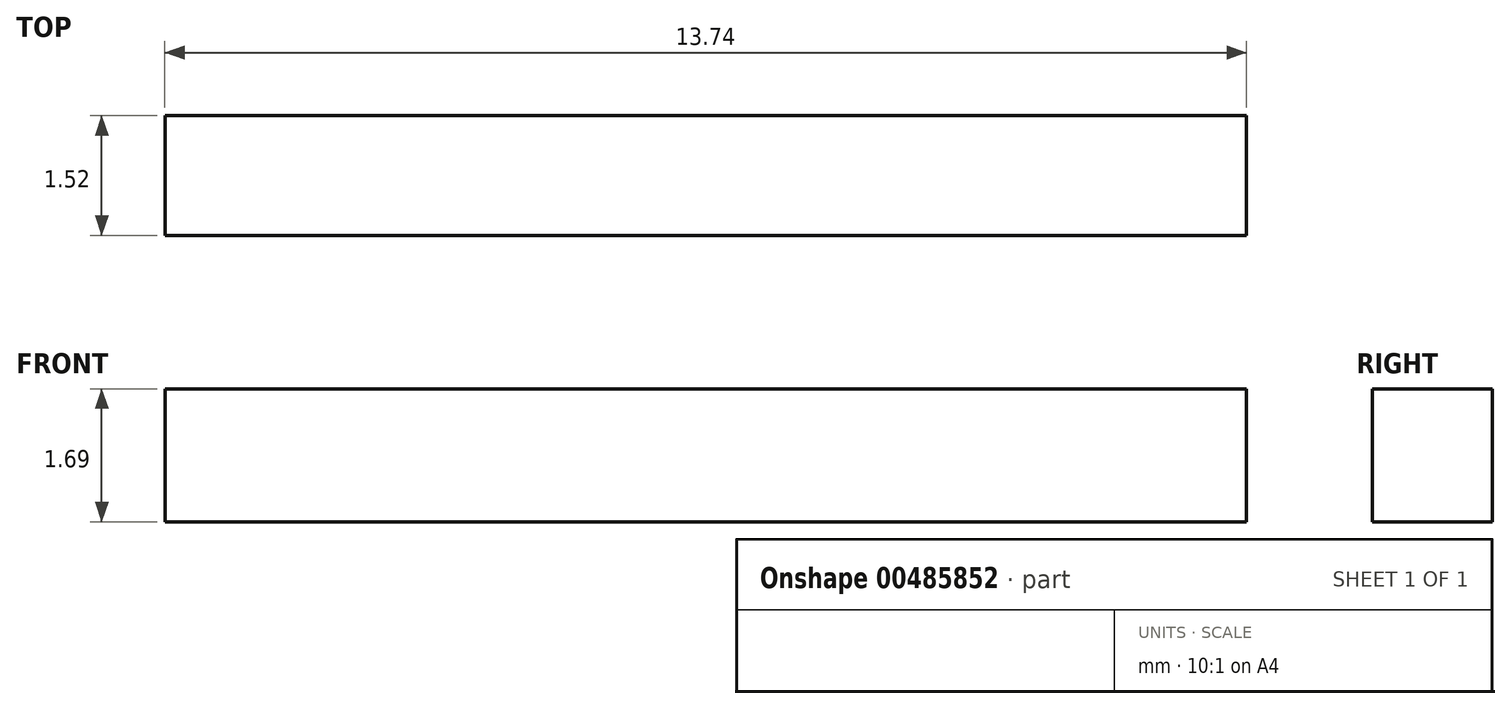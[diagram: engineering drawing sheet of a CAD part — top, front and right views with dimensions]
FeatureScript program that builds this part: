
annotation { "Feature Type Name" : "Feature", "Feature Type Description" : "" }
export const myFeature = defineFeature(function(context is Context, id is Id, definition is map)
    precondition{}
    {
        {
            var Q0;
            Q0=qCreatedBy(makeId("Front.planeOp"),FACE);
            var sketch = newSketch(context, id + "F0", { "sketchPlane" : qUnion([Q0])});
            skLineSegment(sketch, "E0.bottom", {"start": v(-40.49, 18.56) * mm, "end": v(-26.75, 18.56) * mm});
            skLineSegment(sketch, "E0.top", {"start": v(-40.49, 16.87) * mm, "end": v(-26.75, 16.87) * mm});
            skLineSegment(sketch, "E0.left", {"start": v(-40.49, 18.56) * mm, "end": v(-40.49, 16.87) * mm});
            skLineSegment(sketch, "E0.right", {"start": v(-26.75, 18.56) * mm, "end": v(-26.75, 16.87) * mm});
            skSolve(sketch);
        }
        {
            var Q0;
            Q0=makeQuery(id+"F0.imprint","IMPRINT",FACE,{"disambiguationData":[TD([[makeQuery(id+"F0.imprint","IMPRINT",EDGE,{"derivedFrom":sQuery(id+"F0.wireOp",EDGE,"E0.bottom")}),-1.0]])]});
            extrude(context, id + "F1", {"entities" : qUnion([Q0]), "depth" : 1.52 * mm});
        }
    });
